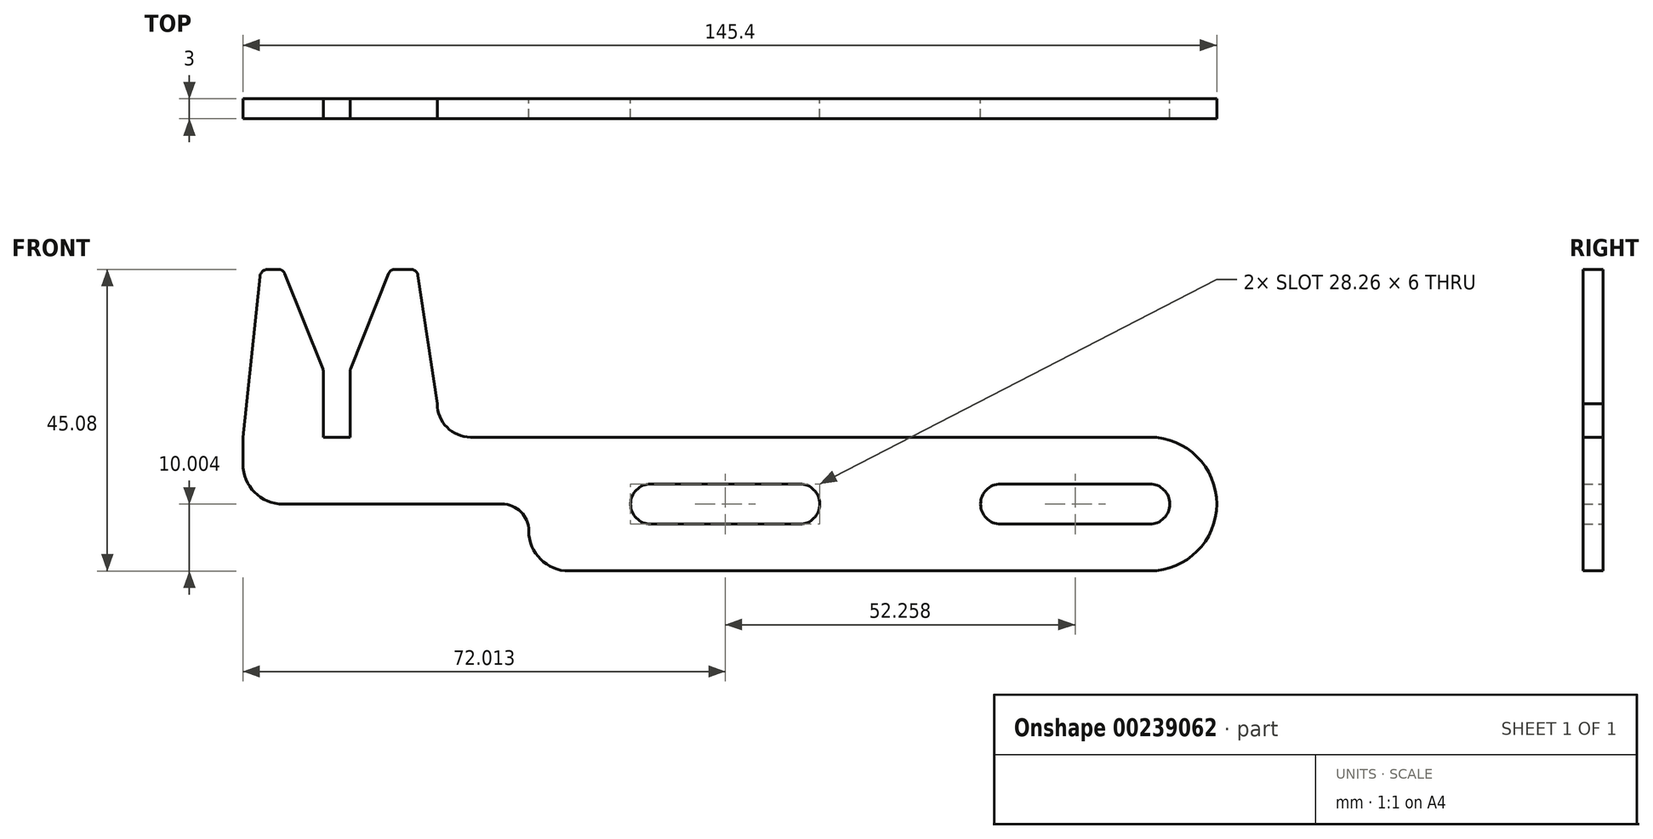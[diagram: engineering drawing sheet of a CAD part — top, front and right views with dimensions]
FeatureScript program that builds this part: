
annotation { "Feature Type Name" : "Feature", "Feature Type Description" : "" }
export const myFeature = defineFeature(function(context is Context, id is Id, definition is map)
    precondition{}
    {
        {
            var Q0;
            Q0=qCreatedBy(makeId("Front.planeOp"),FACE);
            var sketch = newSketch(context, id + "F0", { "sketchPlane" : qUnion([Q0])});
            skLineSegment(sketch, "E0.bottom", {"start": v(-34.44, 6.36) * mm, "end": v(66.96, 6.36) * mm});
            skLineSegment(sketch, "E0.top", {"start": v(-19.76, -13.64) * mm, "end": v(66.96, -13.64) * mm});
            skLineSegment(sketch, "E0.left", {"start": v(-68.44, 6.36) * mm, "end": v(-68.44, 2.36) * mm});
            skPoint(sketch, "E1.visualSharp", {"position": v(81.56, 6.36) * mm});
            skPoint(sketch, "E2.visualSharp", {"position": v(81.56, -13.64) * mm});
            skPoint(sketch, "E3.visualSharp", {"position": v(-68.44, -13.64) * mm});
            skArc(sketch, "E4", {"start": v(66.96, -6.64) * mm, "mid": v(69.96, -3.64) * mm, "end": v(66.96, -0.64) * mm});
            skArc(sketch, "E5", {"start": v(44.7, -0.64) * mm, "mid": v(41.7, -3.64) * mm, "end": v(44.7, -6.64) * mm});
            skArc(sketch, "E6", {"start": v(66.96, -13.64) * mm, "mid": v(76.96, -3.64) * mm, "end": v(66.96, 6.36) * mm});
            skLineSegment(sketch, "E7", {"start": v(44.7, -0.64) * mm, "end": v(66.96, -0.64) * mm});
            skLineSegment(sketch, "E8", {"start": v(66.96, -6.64) * mm, "end": v(44.7, -6.64) * mm});
            skArc(sketch, "E9.MirrorCS", {"start": v(-7.56, -6.64) * mm, "mid": v(-10.56, -3.64) * mm, "end": v(-7.56, -0.64) * mm});
            skArc(sketch, "E10.MirrorCS", {"start": v(14.7, -0.64) * mm, "mid": v(17.7, -3.64) * mm, "end": v(14.7, -6.64) * mm});
            skLineSegment(sketch, "E11.MirrorCS", {"start": v(14.7, -0.64) * mm, "end": v(-7.56, -0.64) * mm});
            skLineSegment(sketch, "E12.MirrorCS", {"start": v(-7.56, -6.64) * mm, "end": v(14.7, -6.64) * mm});
            skLineSegment(sketch, "E13.top", {"start": v(-64.7, 31.44) * mm, "end": v(-63.15, 31.44) * mm});
            skPoint(sketch, "E14.visualSharp", {"position": v(-38.44, 6.36) * mm});
            skArc(sketch, "E14.filletArc", {"start": v(-39.44, 11.36) * mm, "mid": v(-37.97, 7.83) * mm, "end": v(-34.44, 6.36) * mm});
            skLineSegment(sketch, "E15", {"start": v(-56.44, 16.16) * mm, "end": v(-56.44, 6.36) * mm});
            skLineSegment(sketch, "E16", {"start": v(-52.44, 16.16) * mm, "end": v(-52.44, 6.36) * mm});
            skLineSegment(sketch, "E17.trimOffspring", {"start": v(-45.73, 31.44) * mm, "end": v(-43.34, 31.44) * mm});
            skLineSegment(sketch, "E18", {"start": v(-56.44, 6.36) * mm, "end": v(-52.44, 6.36) * mm});
            skLineSegment(sketch, "E19", {"start": v(-56.51, 16.55) * mm, "end": v(-62.17, 30.78) * mm});
            skLineSegment(sketch, "E20", {"start": v(-52.36, 16.55) * mm, "end": v(-46.7, 30.78) * mm});
            skLineSegment(sketch, "E21", {"start": v(-42.3, 30.55) * mm, "end": v(-39.44, 11.36) * mm});
            skPoint(sketch, "E13.right.end.orphan", {"position": v(-38.44, 31.44) * mm});
            skPoint(sketch, "E22.visualSharp", {"position": v(-42.44, 31.44) * mm});
            skArc(sketch, "E22.filletArc", {"start": v(-42.3, 30.55) * mm, "mid": v(-42.66, 31.19) * mm, "end": v(-43.34, 31.44) * mm});
            skPoint(sketch, "E23.visualSharp", {"position": v(-46.44, 31.44) * mm});
            skArc(sketch, "E23.filletArc", {"start": v(-45.73, 31.44) * mm, "mid": v(-46.31, 31.26) * mm, "end": v(-46.7, 30.78) * mm});
            skPoint(sketch, "E24.visualSharp", {"position": v(-62.44, 31.44) * mm});
            skArc(sketch, "E24.filletArc", {"start": v(-62.17, 30.78) * mm, "mid": v(-62.56, 31.26) * mm, "end": v(-63.15, 31.44) * mm});
            skPoint(sketch, "E25.visualSharp", {"position": v(-56.44, 16.36) * mm});
            skArc(sketch, "E25.filletArc", {"start": v(-56.44, 16.16) * mm, "mid": v(-56.46, 16.36) * mm, "end": v(-56.51, 16.55) * mm});
            skPoint(sketch, "E26.visualSharp", {"position": v(-52.44, 16.36) * mm});
            skArc(sketch, "E26.filletArc", {"start": v(-52.36, 16.55) * mm, "mid": v(-52.42, 16.36) * mm, "end": v(-52.44, 16.16) * mm});
            skLineSegment(sketch, "E27", {"start": v(-25.76, -7.64) * mm, "end": v(-25.76, -7.64) * mm});
            skLineSegment(sketch, "E28.trimOffspring", {"start": v(-29.76, -3.64) * mm, "end": v(-62.44, -3.64) * mm});
            skPoint(sketch, "E29.visualSharp", {"position": v(-25.76, -13.64) * mm});
            skArc(sketch, "E29.filletArc", {"start": v(-25.76, -7.64) * mm, "mid": v(-24, -11.88) * mm, "end": v(-19.76, -13.64) * mm});
            skPoint(sketch, "E30.visualSharp", {"position": v(-68.44, -3.64) * mm});
            skArc(sketch, "E30.filletArc", {"start": v(-68.44, 2.36) * mm, "mid": v(-66.68, -1.88) * mm, "end": v(-62.44, -3.64) * mm});
            skPoint(sketch, "E31.visualSharp", {"position": v(-25.76, -3.64) * mm});
            skArc(sketch, "E31.filletArc", {"start": v(-25.76, -7.64) * mm, "mid": v(-26.93, -4.8) * mm, "end": v(-29.76, -3.64) * mm});
            skLineSegment(sketch, "E32", {"start": v(-65.9, 30.35) * mm, "end": v(-68.44, 6.36) * mm});
            skPoint(sketch, "E33.orphan", {"position": v(-68.44, 31.44) * mm});
            skPoint(sketch, "E34.visualSharp", {"position": v(-65.8, 31.44) * mm});
            skArc(sketch, "E34.filletArc", {"start": v(-64.7, 31.44) * mm, "mid": v(-65.51, 31.13) * mm, "end": v(-65.9, 30.35) * mm});
            skSolve(sketch);
        }
        {
            var Q0;
            Q0 = qSketchRegion(id + "F0", true);
            extrude(context, id + "F1", {"entities" : qUnion([Q0]), "depth" : 3 * mm, "offsetDistance" : 25 * mm});
        }
    });
